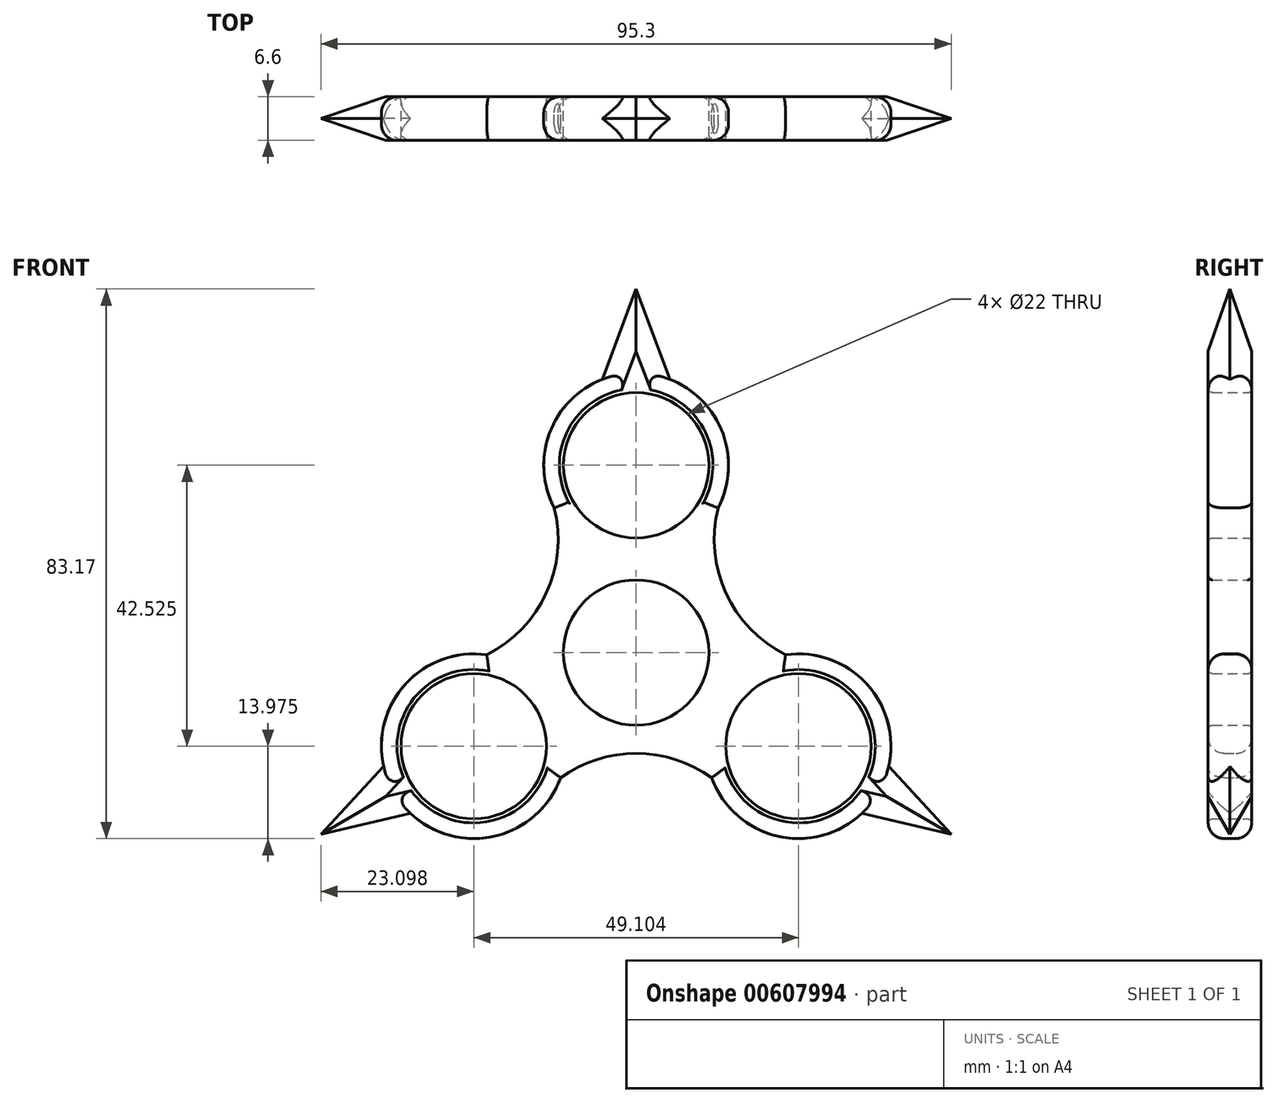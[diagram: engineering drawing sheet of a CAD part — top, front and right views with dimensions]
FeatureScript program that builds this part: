
annotation { "Feature Type Name" : "Feature", "Feature Type Description" : "" }
export const myFeature = defineFeature(function(context is Context, id is Id, definition is map)
    precondition{}
    {
        {
            var Q0;
            Q0=qCreatedBy(makeId("Front.planeOp"),FACE);
            var sketch = newSketch(context, id + "F0", { "sketchPlane" : qUnion([Q0])});
            skCircle(sketch, "E0", {"center": v(0, 0) * mm, "radius": 11 * mm});
            skCircle(sketch, "E1", {"center": v(0, 28.35) * mm, "radius": 11 * mm});
            skCircle(sketch, "E2", {"center": v(24.55, -14.17) * mm, "radius": 11 * mm});
            skCircle(sketch, "E3", {"center": v(-24.55, -14.17) * mm, "radius": 11 * mm});
            skLineSegment(sketch, "E4", {"start": v(0, 28.35) * mm, "end": v(0, 0) * mm});
            skLineSegment(sketch, "E5", {"start": v(24.55, -14.18) * mm, "end": v(0, 0) * mm});
            skLineSegment(sketch, "E6", {"start": v(-24.55, -14.17) * mm, "end": v(0, 0) * mm});
            skArc(sketch, "E7", {"start": v(-5.57, 15.54) * mm, "mid": v(-9.78, 13.3) * mm, "end": v(-13.17, 9.96) * mm});
            skCircle(sketch, "E8", {"center": v(0, 28.35) * mm, "radius": 13.97 * mm});
            skCircle(sketch, "E9", {"center": v(24.55, -14.17) * mm, "radius": 13.97 * mm});
            skCircle(sketch, "E10", {"center": v(-24.55, -14.17) * mm, "radius": 13.97 * mm});
            skArc(sketch, "E11.trimOffspring", {"start": v(16.25, -2.94) * mm, "mid": v(16.45, 1.43) * mm, "end": v(15.5, 5.7) * mm});
            skArc(sketch, "E12.trimOffspring", {"start": v(-10.67, -12.6) * mm, "mid": v(-7.84, -14.53) * mm, "end": v(-4.68, -15.83) * mm});
            skPoint(sketch, "E13", {"position": v(12.39, 21.9) * mm});
            skPoint(sketch, "E14", {"position": v(-12.39, 21.9) * mm});
            skPoint(sketch, "E15", {"position": v(-22.6, -0.34) * mm});
            skPoint(sketch, "E16", {"position": v(-11.42, -18.95) * mm});
            skPoint(sketch, "E17", {"position": v(11.42, -18.95) * mm});
            skPoint(sketch, "E18", {"position": v(22.6, -0.34) * mm});
            skArc(sketch, "E19", {"start": v(12.39, 21.9) * mm, "mid": v(13.59, 8.98) * mm, "end": v(22.6, -0.34) * mm});
            skArc(sketch, "E20", {"start": v(11.42, -18.95) * mm, "mid": v(0, -15.27) * mm, "end": v(-11.42, -18.95) * mm});
            skArc(sketch, "E21", {"start": v(-22.6, -0.34) * mm, "mid": v(-13.59, 8.98) * mm, "end": v(-12.39, 21.9) * mm});
            skArc(sketch, "E22.trimOffspring", {"start": v(-15.5, 5.7) * mm, "mid": v(-16.45, 1.43) * mm, "end": v(-16.25, -2.94) * mm});
            skArc(sketch, "E23.trimOffspring", {"start": v(13.17, 9.96) * mm, "mid": v(9.78, 13.3) * mm, "end": v(5.57, 15.54) * mm});
            skArc(sketch, "E24.trimOffspring", {"start": v(4.68, -15.83) * mm, "mid": v(7.84, -14.53) * mm, "end": v(10.67, -12.6) * mm});
            skLineSegment(sketch, "E25", {"start": v(0, 42.32) * mm, "end": v(0, 55.02) * mm});
            skLineSegment(sketch, "E26", {"start": v(-36.65, -21.16) * mm, "end": v(-47.65, -27.5) * mm});
            skLineSegment(sketch, "E27", {"start": v(36.65, -21.16) * mm, "end": v(47.65, -27.5) * mm});
            skLineSegment(sketch, "E28", {"start": v(-47.65, -27.5) * mm, "end": v(-38.18, -17.24) * mm});
            skLineSegment(sketch, "E29", {"start": v(-47.65, -27.5) * mm, "end": v(-34.16, -24.32) * mm});
            skLineSegment(sketch, "E30", {"start": v(5.11, 41.35) * mm, "end": v(0, 55.02) * mm});
            skLineSegment(sketch, "E31", {"start": v(34.16, -24.32) * mm, "end": v(47.65, -27.5) * mm});
            skLineSegment(sketch, "E32.trimOffspring", {"start": v(38.18, -17.24) * mm, "end": v(47.65, -27.51) * mm});
            skLineSegment(sketch, "E33.trimOffspring", {"start": v(-5.11, 41.35) * mm, "end": v(0, 55.02) * mm});
            skSolve(sketch);
        }
        {
            var Q0;
            Q0 = qSketchRegion(id + "F0", true);
            extrude(context, id + "F1", {"entities" : qUnion([Q0]), "depth" : 6.6 * mm, "offsetDistance" : 25.4 * mm});
        }
        {
            var Q0;
            Q0=makeQuery(id+"F1.opExtrude","CAP_EDGE",EDGE,{"disambiguationData":[OSD([sQuery(id+"F0.wireOp",EDGE,"E8")])],"isStart":false});
            var Q1;
            Q1=makeQuery(id+"F1.opExtrude","CAP_EDGE",EDGE,{"disambiguationData":[OSD([sQuery(id+"F0.wireOp",EDGE,"E21")])],"isStart":false});
            var Q2;
            Q2=makeQuery(id+"F1.opExtrude","CAP_EDGE",EDGE,{"disambiguationData":[OSD([sQuery(id+"F0.wireOp",EDGE,"E19")])],"isStart":false});
            var Q3;
            Q3=makeQuery(id+"F1.opExtrude","CAP_EDGE",EDGE,{"disambiguationData":[OSD([sQuery(id+"F0.wireOp",EDGE,"E9")])],"isStart":false});
            var Q4;
            Q4=makeQuery(id+"F1.opExtrude","CAP_EDGE",EDGE,{"disambiguationData":[OSD([sQuery(id+"F0.wireOp",EDGE,"E20")])],"isStart":false});
            var Q5;
            Q5=makeQuery(id+"F1.opExtrude","CAP_EDGE",EDGE,{"disambiguationData":[OSD([sQuery(id+"F0.wireOp",EDGE,"E10")])],"isStart":false});
            var Q6;
            Q6=makeQuery(id+"F1.opExtrude","CAP_EDGE",EDGE,{"disambiguationData":[OSD([sQuery(id+"F0.wireOp",EDGE,"E8")])],"isStart":true});
            var Q7;
            Q7=makeQuery(id+"F1.opExtrude","CAP_EDGE",EDGE,{"disambiguationData":[OSD([sQuery(id+"F0.wireOp",EDGE,"E21")])],"isStart":true});
            var Q8;
            Q8=makeQuery(id+"F1.opExtrude","CAP_EDGE",EDGE,{"disambiguationData":[OSD([sQuery(id+"F0.wireOp",EDGE,"E19")])],"isStart":true});
            var Q9;
            Q9=makeQuery(id+"F1.opExtrude","CAP_EDGE",EDGE,{"disambiguationData":[OSD([sQuery(id+"F0.wireOp",EDGE,"E20")])],"isStart":true});
            var Q10;
            Q10=makeQuery(id+"F1.opExtrude","CAP_EDGE",EDGE,{"disambiguationData":[OSD([sQuery(id+"F0.wireOp",EDGE,"E10")])],"isStart":true});
            var Q11;
            Q11=makeQuery(id+"F1.opExtrude","CAP_EDGE",EDGE,{"disambiguationData":[OSD([sQuery(id+"F0.wireOp",EDGE,"E9")])],"isStart":true});
            fillet(context, id + "F2", {"entities" : qUnion([Q0, Q1, Q2, Q3, Q4, Q5, Q6, Q7, Q8, Q9, Q10, Q11]), "radius" : 2.41 * mm, "tangentPropagation" : true, "allowEdgeOverflow" : false});
        }
        {
            var Q0;
            Q0=makeQuery(id+"F1.opExtrude","CAP_EDGE",EDGE,{"disambiguationData":[OSD([sQuery(id+"F0.wireOp",EDGE,"E2")])],"isStart":false});
            var Q1;
            Q1=makeQuery(id+"F1.opExtrude","CAP_EDGE",EDGE,{"disambiguationData":[OSD([sQuery(id+"F0.wireOp",EDGE,"E2")])],"isStart":true});
            var Q2;
            Q2=makeQuery(id+"F1.opExtrude","CAP_EDGE",EDGE,{"disambiguationData":[OSD([sQuery(id+"F0.wireOp",EDGE,"E0")])],"isStart":false});
            var Q3;
            Q3=makeQuery(id+"F1.opExtrude","CAP_EDGE",EDGE,{"disambiguationData":[OSD([sQuery(id+"F0.wireOp",EDGE,"E0")])],"isStart":true});
            var Q4;
            Q4=makeQuery(id+"F1.opExtrude","CAP_EDGE",EDGE,{"disambiguationData":[OSD([sQuery(id+"F0.wireOp",EDGE,"E1")])],"isStart":false});
            var Q5;
            Q5=makeQuery(id+"F1.opExtrude","CAP_EDGE",EDGE,{"disambiguationData":[OSD([sQuery(id+"F0.wireOp",EDGE,"E1")])],"isStart":true});
            var Q6;
            Q6=makeQuery(id+"F1.opExtrude","CAP_EDGE",EDGE,{"disambiguationData":[OSD([sQuery(id+"F0.wireOp",EDGE,"E3")])],"isStart":false});
            var Q7;
            Q7=makeQuery(id+"F1.opExtrude","CAP_EDGE",EDGE,{"disambiguationData":[OSD([sQuery(id+"F0.wireOp",EDGE,"E3")])],"isStart":true});
            fillet(context, id + "F3", {"entities" : qUnion([Q0, Q1, Q2, Q3, Q4, Q5, Q6, Q7]), "radius" : 0.64 * mm, "tangentPropagation" : true, "allowEdgeOverflow" : false});
        }
        {
            var Q0;
            Q0=makeQuery(id+"F1.opExtrude","CAP_EDGE",EDGE,{"disambiguationData":[OSD([sQuery(id+"F0.wireOp",EDGE,"E30")])],"isStart":true});
            var Q1;
            Q1=makeQuery(id+"F1.opExtrude","CAP_EDGE",EDGE,{"disambiguationData":[OSD([sQuery(id+"F0.wireOp",EDGE,"E33.trimOffspring")])],"isStart":true});
            var Q2;
            Q2=makeQuery(id+"F1.opExtrude","CAP_EDGE",EDGE,{"disambiguationData":[OSD([sQuery(id+"F0.wireOp",EDGE,"E30")])],"isStart":false});
            var Q3;
            Q3=makeQuery(id+"F1.opExtrude","CAP_EDGE",EDGE,{"disambiguationData":[OSD([sQuery(id+"F0.wireOp",EDGE,"E33.trimOffspring")])],"isStart":false});
            var Q4;
            Q4=makeQuery(id+"F1.opExtrude","CAP_EDGE",EDGE,{"disambiguationData":[OSD([sQuery(id+"F0.wireOp",EDGE,"E28")])],"isStart":true});
            var Q5;
            Q5=makeQuery(id+"F1.opExtrude","CAP_EDGE",EDGE,{"disambiguationData":[OSD([sQuery(id+"F0.wireOp",EDGE,"E29")])],"isStart":true});
            var Q6;
            Q6=makeQuery(id+"F1.opExtrude","CAP_EDGE",EDGE,{"disambiguationData":[OSD([sQuery(id+"F0.wireOp",EDGE,"E28")])],"isStart":false});
            var Q7;
            Q7=makeQuery(id+"F1.opExtrude","CAP_EDGE",EDGE,{"disambiguationData":[OSD([sQuery(id+"F0.wireOp",EDGE,"E29")])],"isStart":false});
            var Q8;
            Q8=makeQuery(id+"F1.opExtrude","CAP_EDGE",EDGE,{"disambiguationData":[OSD([sQuery(id+"F0.wireOp",EDGE,"E31")])],"isStart":false});
            var Q9;
            Q9=makeQuery(id+"F1.opExtrude","CAP_EDGE",EDGE,{"disambiguationData":[OSD([sQuery(id+"F0.wireOp",EDGE,"E32.trimOffspring")])],"isStart":false});
            var Q10;
            Q10=makeQuery(id+"F1.opExtrude","CAP_EDGE",EDGE,{"disambiguationData":[OSD([sQuery(id+"F0.wireOp",EDGE,"E31")])],"isStart":true});
            var Q11;
            Q11=makeQuery(id+"F1.opExtrude","CAP_EDGE",EDGE,{"disambiguationData":[OSD([sQuery(id+"F0.wireOp",EDGE,"E32.trimOffspring")])],"isStart":true});
            chamfer(context, id + "F4", {"entities" : qUnion([Q0, Q1, Q2, Q3, Q4, Q5, Q6, Q7, Q8, Q9, Q10, Q11]), "width" : 3.3 * mm, "tangentPropagation" : true});
        }
    });
